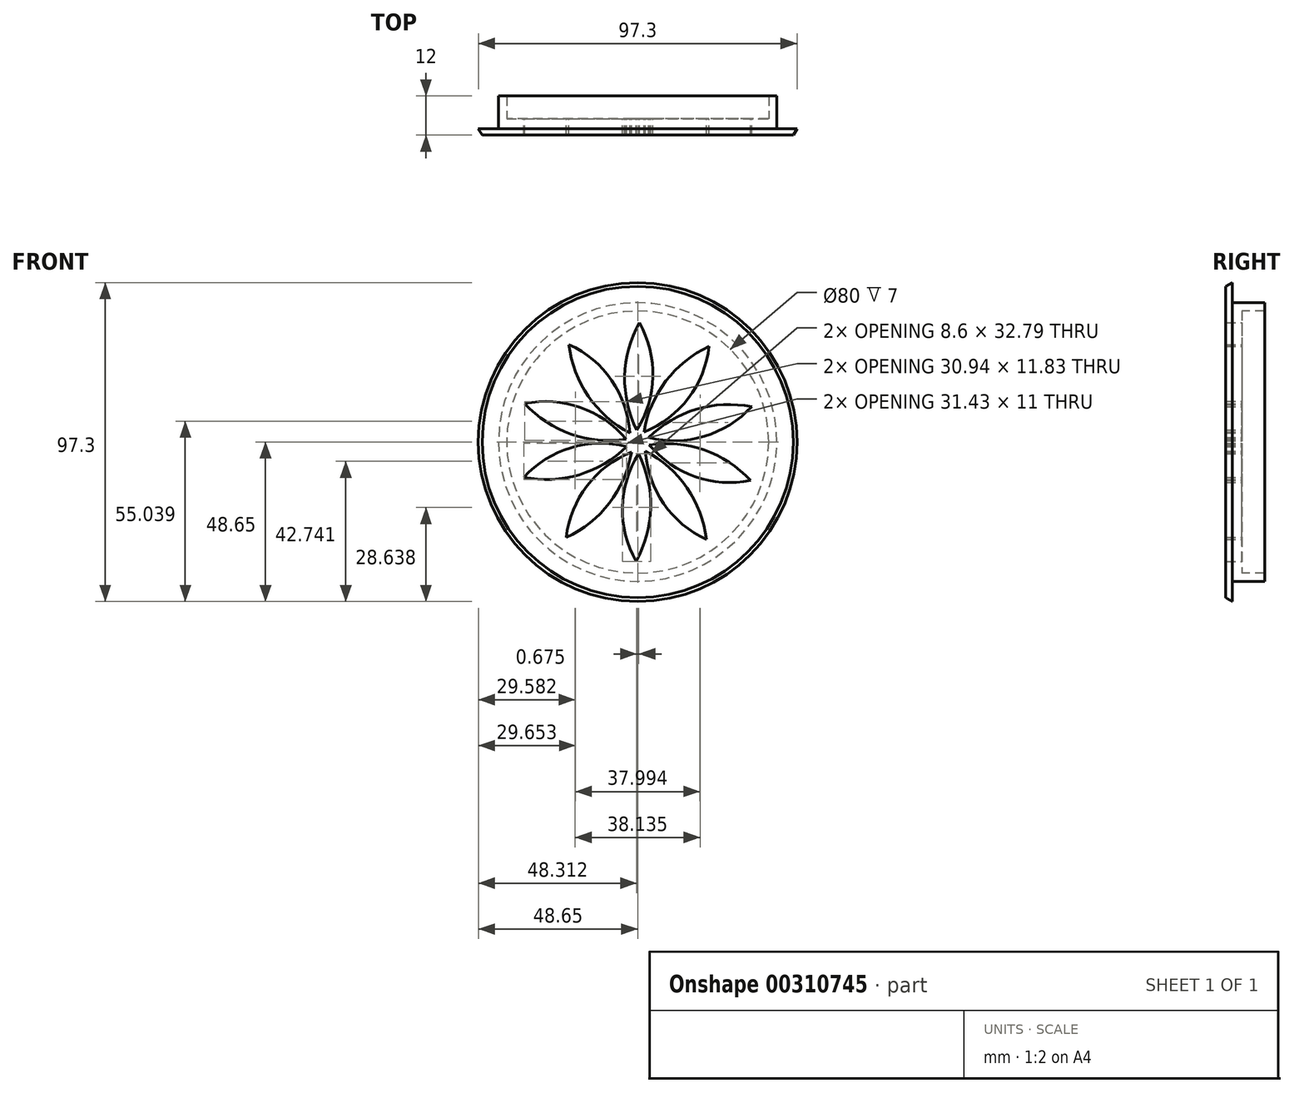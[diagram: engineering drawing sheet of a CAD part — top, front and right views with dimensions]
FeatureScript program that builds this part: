
annotation { "Feature Type Name" : "Feature", "Feature Type Description" : "" }
export const myFeature = defineFeature(function(context is Context, id is Id, definition is map)
    precondition{}
    {
        {
            var Q0;
            Q0=qCreatedBy(makeId("Front.planeOp"),FACE);
            var sketch = newSketch(context, id + "F0", { "sketchPlane" : qUnion([Q0])});
            skCircle(sketch, "E0", {"center": v(0, 0) * mm, "radius": 47.5 * mm});
            skSolve(sketch);
        }
        {
            var Q0;
            Q0=makeQuery(id+"F0.imprint","IMPRINT",FACE,{"disambiguationData":[TD([[makeQuery(id+"F0.imprint","IMPRINT",EDGE,{"derivedFrom":sQuery(id+"F0.wireOp",EDGE,"E0")}),1.0]])]});
            extrude(context, id + "F1", {"entities" : qUnion([Q0]), "oppositeDirection" : true, "depth" : 2 * mm, "hasDraft" : true, "draftAngle" : 30 * degree});
        }
        {
            var Q0;
            Q0=makeQuery(id+"F1.opExtrude","CAP_FACE",FACE,{"disambiguationData":[OSD([sQuery(id+"F0.wireOp",EDGE,"E0")])],"isStart":false});
            var sketch = newSketch(context, id + "F2", { "sketchPlane" : qUnion([Q0])});
            skCircle(sketch, "E1", {"center": v(0, 0) * mm, "radius": 42.5 * mm});
            skCircle(sketch, "E2", {"center": v(0, 0) * mm, "radius": 40 * mm});
            skSolve(sketch);
        }
        {
            var Q0;
            Q0=makeQuery(id+"F2.imprint","IMPRINT",FACE,{"disambiguationData":[TD([[makeQuery(id+"F2.imprint","IMPRINT",EDGE,{"derivedFrom":sQuery(id+"F2.wireOp",EDGE,"E1")}),1.0]])]});
            extrude(context, id + "F3", {"entities" : qUnion([Q0]), "operationType" : NewBodyOperationType.ADD, "depth" : 10 * mm});
        }
        {
            var Q0;
            Q0=makeQuery(id+"F3.boolean.opBoolean","SPLIT",FACE,{"disambiguationData":[TD([makeQuery(id+"F3.opExtrude","SWEPT_FACE",FACE,{"disambiguationData":[OSD([sQuery(id+"F2.wireOp",EDGE,"E2")])]})])],"derivedFrom":makeQuery(id+"F1.opExtrude","CAP_FACE",FACE,{"disambiguationData":[OSD([sQuery(id+"F0.wireOp",EDGE,"E0")])],"isStart":false})});
            var sketch = newSketch(context, id + "F4", { "sketchPlane" : qUnion([Q0])});
            skArc(sketch, "E3", {"start": v(0.28, 3.62) * mm, "mid": v(3.96, 20.11) * mm, "end": v(-0.5, 36.4) * mm});
            skArc(sketch, "E4", {"start": v(-0.5, 36.4) * mm, "mid": v(-4.64, 19.9) * mm, "end": v(0.28, 3.62) * mm});
            skArc(sketch, "E5.1.0", {"start": v(-1.9, 3.1) * mm, "mid": v(-8.61, 18.6) * mm, "end": v(-21.81, 29.15) * mm});
            skArc(sketch, "E5.1.1", {"start": v(-21.81, 29.15) * mm, "mid": v(-15.45, 13.37) * mm, "end": v(-1.9, 3.1) * mm});
            skArc(sketch, "E5.2.0", {"start": v(-3.35, 1.38) * mm, "mid": v(-17.9, 9.99) * mm, "end": v(-34.78, 10.77) * mm});
            skArc(sketch, "E5.2.1", {"start": v(-34.78, 10.77) * mm, "mid": v(-20.36, 1.74) * mm, "end": v(-3.35, 1.38) * mm});
            skArc(sketch, "E5.3.0", {"start": v(-3.53, -0.85) * mm, "mid": v(-20.35, -2.44) * mm, "end": v(-34.47, -11.73) * mm});
            skArc(sketch, "E5.3.1", {"start": v(-34.47, -11.73) * mm, "mid": v(-17.5, -10.56) * mm, "end": v(-3.53, -0.85) * mm});
            skArc(sketch, "E5.4.0", {"start": v(-2.35, -2.76) * mm, "mid": v(-15.03, -13.94) * mm, "end": v(-20.99, -29.75) * mm});
            skArc(sketch, "E5.4.1", {"start": v(-20.99, -29.75) * mm, "mid": v(-7.94, -18.83) * mm, "end": v(-2.35, -2.76) * mm});
            skArc(sketch, "E5.5.0", {"start": v(-0.28, -3.62) * mm, "mid": v(-3.96, -20.11) * mm, "end": v(0.5, -36.4) * mm});
            skArc(sketch, "E5.5.1", {"start": v(0.5, -36.4) * mm, "mid": v(4.64, -19.9) * mm, "end": v(-0.28, -3.62) * mm});
            skArc(sketch, "E5.6.0", {"start": v(1.9, -3.1) * mm, "mid": v(8.61, -18.6) * mm, "end": v(21.81, -29.15) * mm});
            skArc(sketch, "E5.6.1", {"start": v(21.81, -29.15) * mm, "mid": v(15.45, -13.37) * mm, "end": v(1.9, -3.1) * mm});
            skArc(sketch, "E5.7.0", {"start": v(3.35, -1.38) * mm, "mid": v(17.9, -9.99) * mm, "end": v(34.78, -10.77) * mm});
            skArc(sketch, "E5.7.1", {"start": v(34.78, -10.77) * mm, "mid": v(20.36, -1.74) * mm, "end": v(3.35, -1.38) * mm});
            skArc(sketch, "E5.8.0", {"start": v(3.53, 0.85) * mm, "mid": v(20.35, 2.44) * mm, "end": v(34.47, 11.73) * mm});
            skArc(sketch, "E5.8.1", {"start": v(34.47, 11.73) * mm, "mid": v(17.5, 10.56) * mm, "end": v(3.53, 0.85) * mm});
            skArc(sketch, "E5.9.0", {"start": v(2.35, 2.76) * mm, "mid": v(15.03, 13.94) * mm, "end": v(20.99, 29.75) * mm});
            skArc(sketch, "E5.9.1", {"start": v(20.99, 29.75) * mm, "mid": v(7.94, 18.83) * mm, "end": v(2.35, 2.76) * mm});
            skPoint(sketch, "E5.center", {"position": v(0, 0) * mm});
            skSolve(sketch);
        }
        {
            var Q0;
            Q0=makeQuery(id+"F4.imprint","IMPRINT",FACE,{"disambiguationData":[TD([[makeQuery(id+"F4.imprint","IMPRINT",EDGE,{"derivedFrom":sQuery(id+"F4.wireOp",EDGE,"E5.9.0")}),1.0]])]});
            var Q1;
            Q1=makeQuery(id+"F4.imprint","IMPRINT",FACE,{"disambiguationData":[TD([[makeQuery(id+"F4.imprint","IMPRINT",EDGE,{"derivedFrom":sQuery(id+"F4.wireOp",EDGE,"E5.8.0")}),1.0]])]});
            var Q2;
            Q2=makeQuery(id+"F4.imprint","IMPRINT",FACE,{"disambiguationData":[TD([[makeQuery(id+"F4.imprint","IMPRINT",EDGE,{"derivedFrom":sQuery(id+"F4.wireOp",EDGE,"E5.7.0")}),1.0]])]});
            var Q3;
            Q3=makeQuery(id+"F4.imprint","IMPRINT",FACE,{"disambiguationData":[TD([[makeQuery(id+"F4.imprint","IMPRINT",EDGE,{"derivedFrom":sQuery(id+"F4.wireOp",EDGE,"E5.6.0")}),1.0]])]});
            var Q4;
            Q4=makeQuery(id+"F4.imprint","IMPRINT",FACE,{"disambiguationData":[TD([[makeQuery(id+"F4.imprint","IMPRINT",EDGE,{"derivedFrom":sQuery(id+"F4.wireOp",EDGE,"E5.5.0")}),1.0]])]});
            var Q5;
            Q5=makeQuery(id+"F4.imprint","IMPRINT",FACE,{"disambiguationData":[TD([[makeQuery(id+"F4.imprint","IMPRINT",EDGE,{"derivedFrom":sQuery(id+"F4.wireOp",EDGE,"E5.4.0")}),1.0]])]});
            var Q6;
            Q6=makeQuery(id+"F4.imprint","IMPRINT",FACE,{"disambiguationData":[TD([[makeQuery(id+"F4.imprint","IMPRINT",EDGE,{"derivedFrom":sQuery(id+"F4.wireOp",EDGE,"E5.3.0")}),1.0]])]});
            var Q7;
            Q7=makeQuery(id+"F4.imprint","IMPRINT",FACE,{"disambiguationData":[TD([[makeQuery(id+"F4.imprint","IMPRINT",EDGE,{"derivedFrom":sQuery(id+"F4.wireOp",EDGE,"E5.1.0")}),1.0]])]});
            var Q8;
            Q8=makeQuery(id+"F4.imprint","IMPRINT",FACE,{"disambiguationData":[TD([[makeQuery(id+"F4.imprint","IMPRINT",EDGE,{"derivedFrom":sQuery(id+"F4.wireOp",EDGE,"E3")}),1.0]])]});
            var Q9;
            Q9=makeQuery(id+"F4.imprint","IMPRINT",FACE,{"disambiguationData":[TD([[makeQuery(id+"F4.imprint","IMPRINT",EDGE,{"derivedFrom":sQuery(id+"F4.wireOp",EDGE,"E5.2.0")}),1.0]])]});
            extrude(context, id + "F5", {"entities" : qUnion([Q0, Q1, Q2, Q3, Q4, Q5, Q6, Q7, Q8, Q9]), "operationType" : NewBodyOperationType.REMOVE, "oppositeDirection" : true, "depth" : 25 * mm});
        }
        {
            var Q0;
            Q0=makeQuery(id+"F3.boolean.opBoolean","SPLIT",FACE,{"disambiguationData":[TD([makeQuery(id+"F3.opExtrude","SWEPT_FACE",FACE,{"disambiguationData":[OSD([sQuery(id+"F2.wireOp",EDGE,"E2")])]})])],"derivedFrom":makeQuery(id+"F1.opExtrude","CAP_FACE",FACE,{"disambiguationData":[OSD([sQuery(id+"F0.wireOp",EDGE,"E0")])],"isStart":false})});
            extrude(context, id + "F6", {"entities" : qUnion([Q0]), "operationType" : NewBodyOperationType.ADD, "depth" : 3 * mm});
        }
    });
